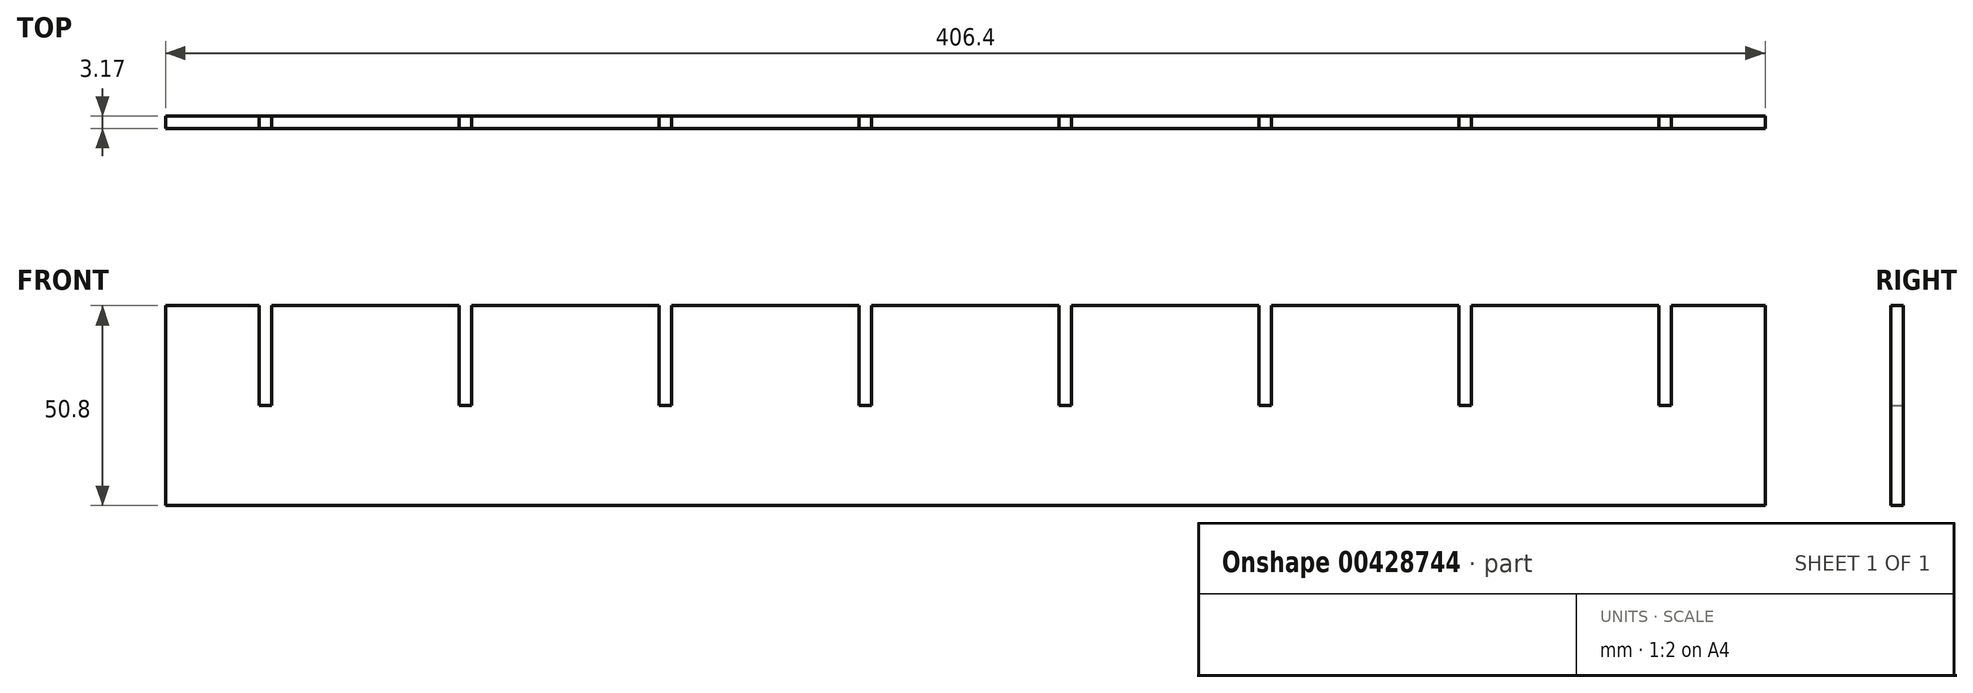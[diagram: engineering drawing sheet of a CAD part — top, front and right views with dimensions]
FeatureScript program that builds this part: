
annotation { "Feature Type Name" : "Feature", "Feature Type Description" : "" }
export const myFeature = defineFeature(function(context is Context, id is Id, definition is map)
    precondition{}
    {
        {
            var Q0;
            Q0=qCreatedBy(makeId("Front.planeOp"),FACE);
            var sketch = newSketch(context, id + "F0", { "sketchPlane" : qUnion([Q0])});
            skLineSegment(sketch, "E0", {"start": v(0, 0) * mm, "end": v(406.4, 0) * mm});
            skLineSegment(sketch, "E1", {"start": v(406.4, 0) * mm, "end": v(406.4, 50.8) * mm});
            skLineSegment(sketch, "E2", {"start": v(0, 0) * mm, "end": v(0, 50.8) * mm});
            skLineSegment(sketch, "E3", {"start": v(0, 50.8) * mm, "end": v(23.81, 50.8) * mm});
            skLineSegment(sketch, "E4", {"start": v(23.81, 50.8) * mm, "end": v(23.81, 25.4) * mm});
            skLineSegment(sketch, "E5", {"start": v(23.81, 25.4) * mm, "end": v(26.99, 25.4) * mm});
            skLineSegment(sketch, "E6", {"start": v(26.99, 25.4) * mm, "end": v(26.99, 50.8) * mm});
            skLineSegment(sketch, "E7", {"start": v(26.99, 50.8) * mm, "end": v(74.61, 50.8) * mm});
            skLineSegment(sketch, "E8", {"start": v(74.61, 50.8) * mm, "end": v(74.61, 25.4) * mm});
            skLineSegment(sketch, "E9", {"start": v(74.61, 25.4) * mm, "end": v(77.79, 25.4) * mm});
            skLineSegment(sketch, "E10", {"start": v(77.79, 25.4) * mm, "end": v(77.79, 50.8) * mm});
            skLineSegment(sketch, "E11", {"start": v(77.79, 50.8) * mm, "end": v(125.41, 50.8) * mm});
            skLineSegment(sketch, "E12", {"start": v(125.41, 50.8) * mm, "end": v(125.41, 25.4) * mm});
            skLineSegment(sketch, "E13", {"start": v(125.41, 25.4) * mm, "end": v(128.59, 25.4) * mm});
            skLineSegment(sketch, "E14", {"start": v(128.59, 25.4) * mm, "end": v(128.59, 50.8) * mm});
            skLineSegment(sketch, "E15", {"start": v(128.59, 50.8) * mm, "end": v(176.21, 50.8) * mm});
            skLineSegment(sketch, "E16", {"start": v(176.21, 50.8) * mm, "end": v(176.21, 25.4) * mm});
            skLineSegment(sketch, "E17", {"start": v(176.21, 25.4) * mm, "end": v(179.39, 25.4) * mm});
            skLineSegment(sketch, "E18", {"start": v(179.39, 25.4) * mm, "end": v(179.39, 50.8) * mm});
            skLineSegment(sketch, "E19", {"start": v(328.61, 25.4) * mm, "end": v(331.79, 25.4) * mm});
            skLineSegment(sketch, "E20", {"start": v(331.79, 25.4) * mm, "end": v(331.79, 50.8) * mm});
            skLineSegment(sketch, "E21", {"start": v(331.79, 50.8) * mm, "end": v(379.41, 50.8) * mm});
            skLineSegment(sketch, "E22", {"start": v(379.41, 50.8) * mm, "end": v(379.41, 25.4) * mm});
            skLineSegment(sketch, "E23", {"start": v(379.41, 25.4) * mm, "end": v(382.59, 25.4) * mm});
            skLineSegment(sketch, "E24", {"start": v(382.59, 25.4) * mm, "end": v(382.59, 50.8) * mm});
            skLineSegment(sketch, "E25", {"start": v(382.59, 50.8) * mm, "end": v(406.4, 50.8) * mm});
            skLineSegment(sketch, "E26", {"start": v(179.39, 50.8) * mm, "end": v(227.01, 50.8) * mm});
            skLineSegment(sketch, "E27", {"start": v(227.01, 50.8) * mm, "end": v(227.01, 25.4) * mm});
            skLineSegment(sketch, "E28", {"start": v(227.01, 25.4) * mm, "end": v(230.19, 25.4) * mm});
            skLineSegment(sketch, "E29", {"start": v(230.19, 25.4) * mm, "end": v(230.19, 50.8) * mm});
            skLineSegment(sketch, "E30", {"start": v(230.19, 50.8) * mm, "end": v(277.81, 50.8) * mm});
            skLineSegment(sketch, "E31", {"start": v(277.81, 50.8) * mm, "end": v(277.81, 25.4) * mm});
            skLineSegment(sketch, "E32", {"start": v(277.81, 25.4) * mm, "end": v(280.99, 25.4) * mm});
            skLineSegment(sketch, "E33", {"start": v(280.99, 25.4) * mm, "end": v(280.99, 50.8) * mm});
            skLineSegment(sketch, "E34", {"start": v(280.99, 50.8) * mm, "end": v(328.61, 50.8) * mm});
            skLineSegment(sketch, "E35", {"start": v(328.61, 50.8) * mm, "end": v(328.61, 25.4) * mm});
            skSolve(sketch);
        }
        {
            var Q0;
            Q0=makeQuery(id+"F0.imprint","IMPRINT",FACE,{"disambiguationData":[TD([[makeQuery(id+"F0.imprint","IMPRINT",EDGE,{"derivedFrom":sQuery(id+"F0.wireOp",EDGE,"E0")}),1.0]])]});
            extrude(context, id + "F1", {"entities" : qUnion([Q0]), "depth" : 3.17 * mm});
        }
    });
